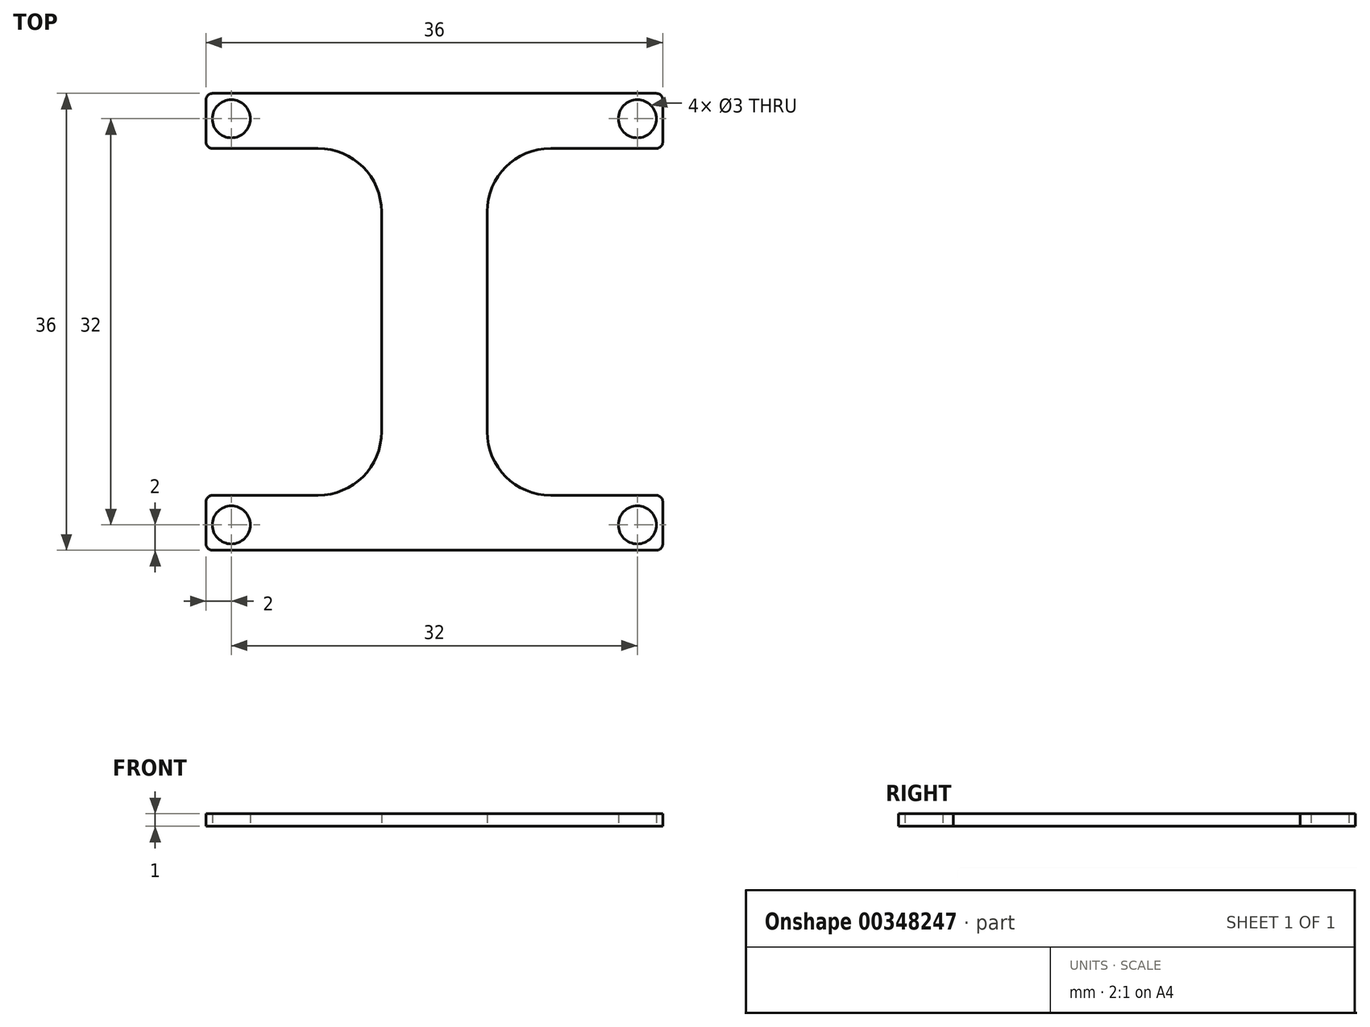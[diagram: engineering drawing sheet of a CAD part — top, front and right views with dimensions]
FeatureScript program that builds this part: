
annotation { "Feature Type Name" : "Feature", "Feature Type Description" : "" }
export const myFeature = defineFeature(function(context is Context, id is Id, definition is map)
    precondition{}
    {
        {
            var Q0;
            Q0=qCreatedBy(makeId("Top.planeOp"),FACE);
            var sketch = newSketch(context, id + "F0", { "sketchPlane" : qUnion([Q0])});
            skLineSegment(sketch, "E0.bottom", {"start": v(17.5, -18) * mm, "end": v(-17.5, -18) * mm});
            skLineSegment(sketch, "E0.top", {"start": v(17.5, 18) * mm, "end": v(-17.5, 18) * mm});
            skLineSegment(sketch, "E0.left", {"start": v(18, -17.5) * mm, "end": v(18, -14.17) * mm});
            skLineSegment(sketch, "E0.right", {"start": v(-18, -17.5) * mm, "end": v(-18, -14.17) * mm});
            skPoint(sketch, "E0.middle", {"position": v(0, 0) * mm});
            skLineSegment(sketch, "E1", {"start": v(-17.5, 13.67) * mm, "end": v(-9.17, 13.67) * mm});
            skLineSegment(sketch, "E2.MirrorCS", {"start": v(-17.5, -13.67) * mm, "end": v(-9.17, -13.67) * mm});
            skLineSegment(sketch, "E3", {"start": v(-4.17, 8.67) * mm, "end": v(-4.17, -8.67) * mm});
            skLineSegment(sketch, "E4.MirrorCS", {"start": v(4.17, 8.67) * mm, "end": v(4.17, -8.67) * mm});
            skCircle(sketch, "E5", {"center": v(-16, 16) * mm, "radius": 1.5 * mm});
            skCircle(sketch, "E6.MirrorC", {"center": v(16, 16) * mm, "radius": 1.5 * mm});
            skCircle(sketch, "E7.MirrorC", {"center": v(16, -16) * mm, "radius": 1.5 * mm});
            skCircle(sketch, "E8.MirrorC", {"center": v(-16, -16) * mm, "radius": 1.5 * mm});
            skLineSegment(sketch, "E9.trimOffspring", {"start": v(-18, 14.17) * mm, "end": v(-18, 17.5) * mm});
            skLineSegment(sketch, "E10.trimOffspring", {"start": v(18, 14.17) * mm, "end": v(18, 17.5) * mm});
            skPoint(sketch, "E11.visualSharp", {"position": v(18, 13.67) * mm});
            skArc(sketch, "E11.filletArc", {"start": v(17.5, 13.67) * mm, "mid": v(17.85, 13.82) * mm, "end": v(18, 14.17) * mm});
            skPoint(sketch, "E12.visualSharp", {"position": v(18, 18) * mm});
            skArc(sketch, "E12.filletArc", {"start": v(18, 17.5) * mm, "mid": v(17.85, 17.85) * mm, "end": v(17.5, 18) * mm});
            skPoint(sketch, "E13.visualSharp", {"position": v(-18, 18) * mm});
            skArc(sketch, "E13.filletArc", {"start": v(-17.5, 18) * mm, "mid": v(-17.85, 17.85) * mm, "end": v(-18, 17.5) * mm});
            skPoint(sketch, "E14.visualSharp", {"position": v(-18, 13.67) * mm});
            skArc(sketch, "E14.filletArc", {"start": v(-18, 14.17) * mm, "mid": v(-17.85, 13.82) * mm, "end": v(-17.5, 13.67) * mm});
            skPoint(sketch, "E15.visualSharp", {"position": v(-18, -13.67) * mm});
            skArc(sketch, "E15.filletArc", {"start": v(-17.5, -13.67) * mm, "mid": v(-17.85, -13.82) * mm, "end": v(-18, -14.17) * mm});
            skPoint(sketch, "E16.visualSharp", {"position": v(-18, -18) * mm});
            skArc(sketch, "E16.filletArc", {"start": v(-18, -17.5) * mm, "mid": v(-17.85, -17.85) * mm, "end": v(-17.5, -18) * mm});
            skPoint(sketch, "E17.visualSharp", {"position": v(18, -18) * mm});
            skArc(sketch, "E17.filletArc", {"start": v(17.5, -18) * mm, "mid": v(17.85, -17.85) * mm, "end": v(18, -17.5) * mm});
            skPoint(sketch, "E18.visualSharp", {"position": v(18, -13.67) * mm});
            skArc(sketch, "E18.filletArc", {"start": v(18, -14.17) * mm, "mid": v(17.85, -13.82) * mm, "end": v(17.5, -13.67) * mm});
            skLineSegment(sketch, "E19.trimOffspring", {"start": v(9.17, 13.67) * mm, "end": v(17.5, 13.67) * mm});
            skLineSegment(sketch, "E20.trimOffspring", {"start": v(9.17, -13.67) * mm, "end": v(17.5, -13.67) * mm});
            skPoint(sketch, "E21.visualSharp", {"position": v(-4.17, 13.67) * mm});
            skArc(sketch, "E21.filletArc", {"start": v(-4.17, 8.67) * mm, "mid": v(-5.63, 12.2) * mm, "end": v(-9.17, 13.67) * mm});
            skPoint(sketch, "E22.visualSharp", {"position": v(-4.17, -13.67) * mm});
            skArc(sketch, "E22.filletArc", {"start": v(-9.17, -13.67) * mm, "mid": v(-5.63, -12.2) * mm, "end": v(-4.17, -8.67) * mm});
            skPoint(sketch, "E23.visualSharp", {"position": v(4.17, -13.67) * mm});
            skArc(sketch, "E23.filletArc", {"start": v(4.17, -8.67) * mm, "mid": v(5.63, -12.2) * mm, "end": v(9.17, -13.67) * mm});
            skPoint(sketch, "E24.visualSharp", {"position": v(4.17, 13.67) * mm});
            skArc(sketch, "E24.filletArc", {"start": v(9.17, 13.67) * mm, "mid": v(5.63, 12.2) * mm, "end": v(4.17, 8.67) * mm});
            skSolve(sketch);
        }
        {
            var Q0;
            Q0=makeQuery(id+"F0.imprint","IMPRINT",FACE,{"disambiguationData":[TD([[makeQuery(id+"F0.imprint","IMPRINT",EDGE,{"derivedFrom":sQuery(id+"F0.wireOp",EDGE,"E0.bottom")}),-1.0]])]});
            extrude(context, id + "F1", {"entities" : qUnion([Q0]), "depth" : 1 * mm});
        }
    });
